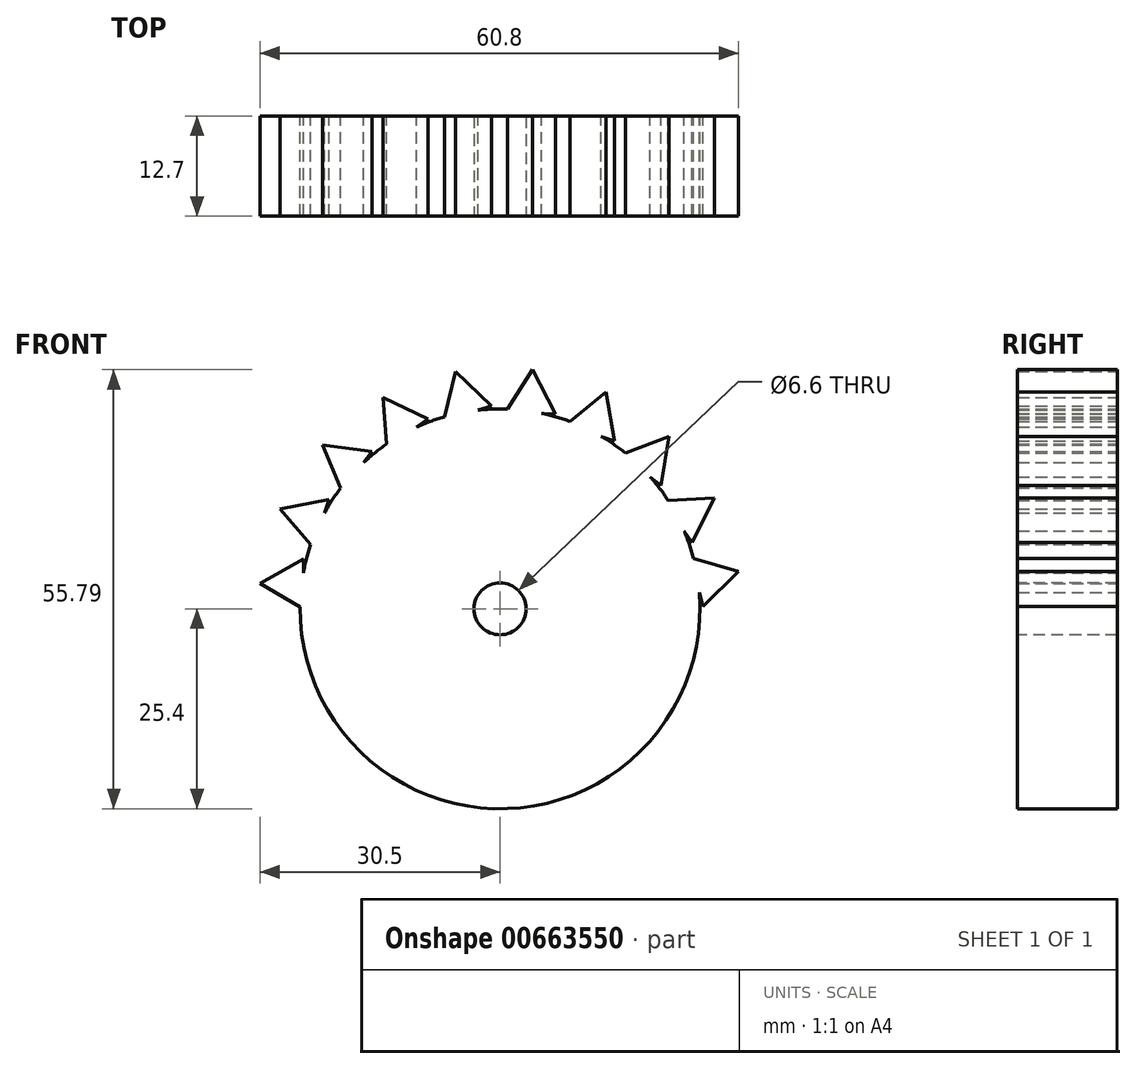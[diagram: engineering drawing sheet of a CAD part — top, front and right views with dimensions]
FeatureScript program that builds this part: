
annotation { "Feature Type Name" : "Feature", "Feature Type Description" : "" }
export const myFeature = defineFeature(function(context is Context, id is Id, definition is map)
    precondition{}
    {
        {
            var Q0;
            Q0=qCreatedBy(makeId("Front.planeOp"),FACE);
            var sketch = newSketch(context, id + "F0", { "sketchPlane" : qUnion([Q0])});
            skCircle(sketch, "E0", {"center": v(0, 0) * mm, "radius": 25.4 * mm});
            skSolve(sketch);
        }
        {
            var Q0;
            Q0=makeQuery(id+"F0.imprint","IMPRINT",FACE,{"disambiguationData":[TD([[makeQuery(id+"F0.imprint","IMPRINT",EDGE,{"derivedFrom":sQuery(id+"F0.wireOp",EDGE,"E0")}),1.0]])]});
            extrude(context, id + "F1", {"entities" : qUnion([Q0]), "depth" : 12.7 * mm, "offsetDistance" : 25.4 * mm});
        }
        {
            var Q0;
            Q0=qCreatedBy(makeId("Front.planeOp"),FACE);
            var sketch = newSketch(context, id + "F2", { "sketchPlane" : qUnion([Q0])});
            skLineSegment(sketch, "E1", {"start": v(-25.04, 0) * mm, "end": v(-30.5, 3.23) * mm});
            skLineSegment(sketch, "E2", {"start": v(-30.5, 3.23) * mm, "end": v(-24.97, 6.35) * mm});
            skLineSegment(sketch, "E3", {"start": v(-24.97, 6.35) * mm, "end": v(-25.04, 0) * mm});
            skLineSegment(sketch, "E4.1.0", {"start": v(-27.94, 12.66) * mm, "end": v(-21.7, 13.88) * mm});
            skLineSegment(sketch, "E4.1.1", {"start": v(-23.77, 7.88) * mm, "end": v(-27.94, 12.66) * mm});
            skLineSegment(sketch, "E4.1.2", {"start": v(-21.7, 13.88) * mm, "end": v(-23.77, 7.88) * mm});
            skLineSegment(sketch, "E4.2.0", {"start": v(-22.53, 20.8) * mm, "end": v(-16.24, 20) * mm});
            skLineSegment(sketch, "E4.2.1", {"start": v(-20.08, 14.95) * mm, "end": v(-22.53, 20.8) * mm});
            skLineSegment(sketch, "E4.2.2", {"start": v(-16.24, 20) * mm, "end": v(-20.08, 14.95) * mm});
            skLineSegment(sketch, "E4.3.0", {"start": v(-14.85, 26.84) * mm, "end": v(-9.12, 24.1) * mm});
            skLineSegment(sketch, "E4.3.1", {"start": v(-14.36, 20.5) * mm, "end": v(-14.85, 26.84) * mm});
            skLineSegment(sketch, "E4.3.2", {"start": v(-9.12, 24.1) * mm, "end": v(-14.36, 20.5) * mm});
            skLineSegment(sketch, "E4.4.0", {"start": v(-5.65, 30.15) * mm, "end": v(-1.08, 25.74) * mm});
            skLineSegment(sketch, "E4.4.1", {"start": v(-7.18, 23.98) * mm, "end": v(-5.65, 30.15) * mm});
            skLineSegment(sketch, "E4.4.2", {"start": v(-1.08, 25.74) * mm, "end": v(-7.18, 23.98) * mm});
            skLineSegment(sketch, "E4.5.0", {"start": v(4.12, 30.4) * mm, "end": v(7.07, 24.77) * mm});
            skLineSegment(sketch, "E4.5.1", {"start": v(0.73, 25.03) * mm, "end": v(4.12, 30.4) * mm});
            skLineSegment(sketch, "E4.5.2", {"start": v(7.07, 24.77) * mm, "end": v(0.73, 25.03) * mm});
            skLineSegment(sketch, "E4.6.0", {"start": v(13.47, 27.56) * mm, "end": v(14.5, 21.3) * mm});
            skLineSegment(sketch, "E4.6.1", {"start": v(8.56, 23.53) * mm, "end": v(13.47, 27.56) * mm});
            skLineSegment(sketch, "E4.6.2", {"start": v(14.5, 21.3) * mm, "end": v(8.56, 23.53) * mm});
            skLineSegment(sketch, "E4.7.0", {"start": v(21.46, 21.92) * mm, "end": v(20.47, 15.65) * mm});
            skLineSegment(sketch, "E4.7.1", {"start": v(15.53, 19.64) * mm, "end": v(21.46, 21.92) * mm});
            skLineSegment(sketch, "E4.7.2", {"start": v(20.47, 15.65) * mm, "end": v(15.53, 19.64) * mm});
            skLineSegment(sketch, "E4.8.0", {"start": v(27.26, 14.06) * mm, "end": v(24.35, 8.41) * mm});
            skLineSegment(sketch, "E4.8.1", {"start": v(20.92, 13.76) * mm, "end": v(27.26, 14.06) * mm});
            skLineSegment(sketch, "E4.8.2", {"start": v(24.35, 8.41) * mm, "end": v(20.92, 13.76) * mm});
            skLineSegment(sketch, "E4.9.0", {"start": v(30.3, 4.77) * mm, "end": v(25.76, 0.33) * mm});
            skLineSegment(sketch, "E4.9.1", {"start": v(24.18, 6.48) * mm, "end": v(30.3, 4.77) * mm});
            skLineSegment(sketch, "E4.9.2", {"start": v(25.76, 0.33) * mm, "end": v(24.18, 6.48) * mm});
            skPoint(sketch, "E4.center", {"position": v(0, 0) * mm});
            skLineSegment(sketch, "E4.anchor1", {"start": v(0, 0) * mm, "end": v(-30.5, 3.23) * mm, "construction": true});
            skLineSegment(sketch, "E4.anchor2", {"start": v(0, 0) * mm, "end": v(30.3, 4.77) * mm, "construction": true});
            skSolve(sketch);
        }
        {
            var Q0;
            Q0=makeQuery(id+"F2.imprint","IMPRINT",FACE,{"disambiguationData":[TD([[makeQuery(id+"F2.imprint","IMPRINT",EDGE,{"derivedFrom":sQuery(id+"F2.wireOp",EDGE,"E4.1.0")}),-1.0]])]});
            var Q1;
            Q1=makeQuery(id+"F2.imprint","IMPRINT",FACE,{"disambiguationData":[TD([[makeQuery(id+"F2.imprint","IMPRINT",EDGE,{"derivedFrom":sQuery(id+"F2.wireOp",EDGE,"E1")}),-1.0]])]});
            var Q2;
            Q2=makeQuery(id+"F2.imprint","IMPRINT",FACE,{"disambiguationData":[TD([[makeQuery(id+"F2.imprint","IMPRINT",EDGE,{"derivedFrom":sQuery(id+"F2.wireOp",EDGE,"E4.2.0")}),-1.0]])]});
            var Q3;
            Q3=makeQuery(id+"F2.imprint","IMPRINT",FACE,{"disambiguationData":[TD([[makeQuery(id+"F2.imprint","IMPRINT",EDGE,{"derivedFrom":sQuery(id+"F2.wireOp",EDGE,"E4.3.0")}),-1.0]])]});
            var Q4;
            Q4=makeQuery(id+"F2.imprint","IMPRINT",FACE,{"disambiguationData":[TD([[makeQuery(id+"F2.imprint","IMPRINT",EDGE,{"derivedFrom":sQuery(id+"F2.wireOp",EDGE,"E4.4.0")}),-1.0]])]});
            var Q5;
            Q5=makeQuery(id+"F2.imprint","IMPRINT",FACE,{"disambiguationData":[TD([[makeQuery(id+"F2.imprint","IMPRINT",EDGE,{"derivedFrom":sQuery(id+"F2.wireOp",EDGE,"E4.5.0")}),-1.0]])]});
            var Q6;
            Q6=makeQuery(id+"F2.imprint","IMPRINT",FACE,{"disambiguationData":[TD([[makeQuery(id+"F2.imprint","IMPRINT",EDGE,{"derivedFrom":sQuery(id+"F2.wireOp",EDGE,"E4.6.0")}),-1.0]])]});
            var Q7;
            Q7=makeQuery(id+"F2.imprint","IMPRINT",FACE,{"disambiguationData":[TD([[makeQuery(id+"F2.imprint","IMPRINT",EDGE,{"derivedFrom":sQuery(id+"F2.wireOp",EDGE,"E4.7.0")}),-1.0]])]});
            var Q8;
            Q8=makeQuery(id+"F2.imprint","IMPRINT",FACE,{"disambiguationData":[TD([[makeQuery(id+"F2.imprint","IMPRINT",EDGE,{"derivedFrom":sQuery(id+"F2.wireOp",EDGE,"E4.8.0")}),-1.0]])]});
            var Q9;
            Q9=makeQuery(id+"F2.imprint","IMPRINT",FACE,{"disambiguationData":[TD([[makeQuery(id+"F2.imprint","IMPRINT",EDGE,{"derivedFrom":sQuery(id+"F2.wireOp",EDGE,"E4.9.0")}),-1.0]])]});
            extrude(context, id + "F3", {"entities" : qUnion([Q0, Q1, Q2, Q3, Q4, Q5, Q6, Q7, Q8, Q9]), "operationType" : NewBodyOperationType.ADD, "depth" : 12.7 * mm, "offsetDistance" : 25.4 * mm});
        }
        {
            var Q0;
            Q0=makeQuery(id+"F3.boolean.opBoolean","MERGE",FACE,{"derivedFrom":[makeQuery(id+"F1.opExtrude","CAP_FACE",FACE,{"disambiguationData":[OSD([sQuery(id+"F0.wireOp",EDGE,"E0")])],"isStart":false}),makeQuery(id+"F3.opExtrude","CAP_FACE",FACE,{"disambiguationData":[OSD([sQuery(id+"F2.wireOp",EDGE,"E1"),sQuery(id+"F2.wireOp",EDGE,"E2"),sQuery(id+"F2.wireOp",EDGE,"E3")])],"isStart":false}),makeQuery(id+"F3.opExtrude","CAP_FACE",FACE,{"disambiguationData":[OSD([sQuery(id+"F2.wireOp",EDGE,"E4.1.0"),sQuery(id+"F2.wireOp",EDGE,"E4.1.1"),sQuery(id+"F2.wireOp",EDGE,"E4.1.2")])],"isStart":false}),makeQuery(id+"F3.opExtrude","CAP_FACE",FACE,{"disambiguationData":[OSD([sQuery(id+"F2.wireOp",EDGE,"E4.2.0"),sQuery(id+"F2.wireOp",EDGE,"E4.2.1"),sQuery(id+"F2.wireOp",EDGE,"E4.2.2")])],"isStart":false}),makeQuery(id+"F3.opExtrude","CAP_FACE",FACE,{"disambiguationData":[OSD([sQuery(id+"F2.wireOp",EDGE,"E4.3.0"),sQuery(id+"F2.wireOp",EDGE,"E4.3.1"),sQuery(id+"F2.wireOp",EDGE,"E4.3.2")])],"isStart":false}),makeQuery(id+"F3.opExtrude","CAP_FACE",FACE,{"disambiguationData":[OSD([sQuery(id+"F2.wireOp",EDGE,"E4.4.0"),sQuery(id+"F2.wireOp",EDGE,"E4.4.1"),sQuery(id+"F2.wireOp",EDGE,"E4.4.2")])],"isStart":false}),makeQuery(id+"F3.opExtrude","CAP_FACE",FACE,{"disambiguationData":[OSD([sQuery(id+"F2.wireOp",EDGE,"E4.5.0"),sQuery(id+"F2.wireOp",EDGE,"E4.5.1"),sQuery(id+"F2.wireOp",EDGE,"E4.5.2")])],"isStart":false}),makeQuery(id+"F3.opExtrude","CAP_FACE",FACE,{"disambiguationData":[OSD([sQuery(id+"F2.wireOp",EDGE,"E4.6.0"),sQuery(id+"F2.wireOp",EDGE,"E4.6.1"),sQuery(id+"F2.wireOp",EDGE,"E4.6.2")])],"isStart":false}),makeQuery(id+"F3.opExtrude","CAP_FACE",FACE,{"disambiguationData":[OSD([sQuery(id+"F2.wireOp",EDGE,"E4.7.0"),sQuery(id+"F2.wireOp",EDGE,"E4.7.1"),sQuery(id+"F2.wireOp",EDGE,"E4.7.2")])],"isStart":false}),makeQuery(id+"F3.opExtrude","CAP_FACE",FACE,{"disambiguationData":[OSD([sQuery(id+"F2.wireOp",EDGE,"E4.8.0"),sQuery(id+"F2.wireOp",EDGE,"E4.8.1"),sQuery(id+"F2.wireOp",EDGE,"E4.8.2")])],"isStart":false}),makeQuery(id+"F3.opExtrude","CAP_FACE",FACE,{"disambiguationData":[OSD([sQuery(id+"F2.wireOp",EDGE,"E4.9.0"),sQuery(id+"F2.wireOp",EDGE,"E4.9.1"),sQuery(id+"F2.wireOp",EDGE,"E4.9.2")])],"isStart":false})]});
            var sketch = newSketch(context, id + "F4", { "sketchPlane" : qUnion([Q0])});
            skCircle(sketch, "E5", {"center": v(0, 0) * mm, "radius": 3.3 * mm});
            skSolve(sketch);
        }
        {
            var Q0;
            Q0=makeQuery(id+"F4.imprint","IMPRINT",FACE,{"disambiguationData":[TD([[makeQuery(id+"F4.imprint","IMPRINT",EDGE,{"derivedFrom":sQuery(id+"F4.wireOp",EDGE,"E5")}),1.0]])]});
            extrude(context, id + "F5", {"entities" : qUnion([Q0]), "operationType" : NewBodyOperationType.REMOVE, "oppositeDirection" : true, "depth" : 12.7 * mm, "offsetDistance" : 25.4 * mm});
        }
    });
